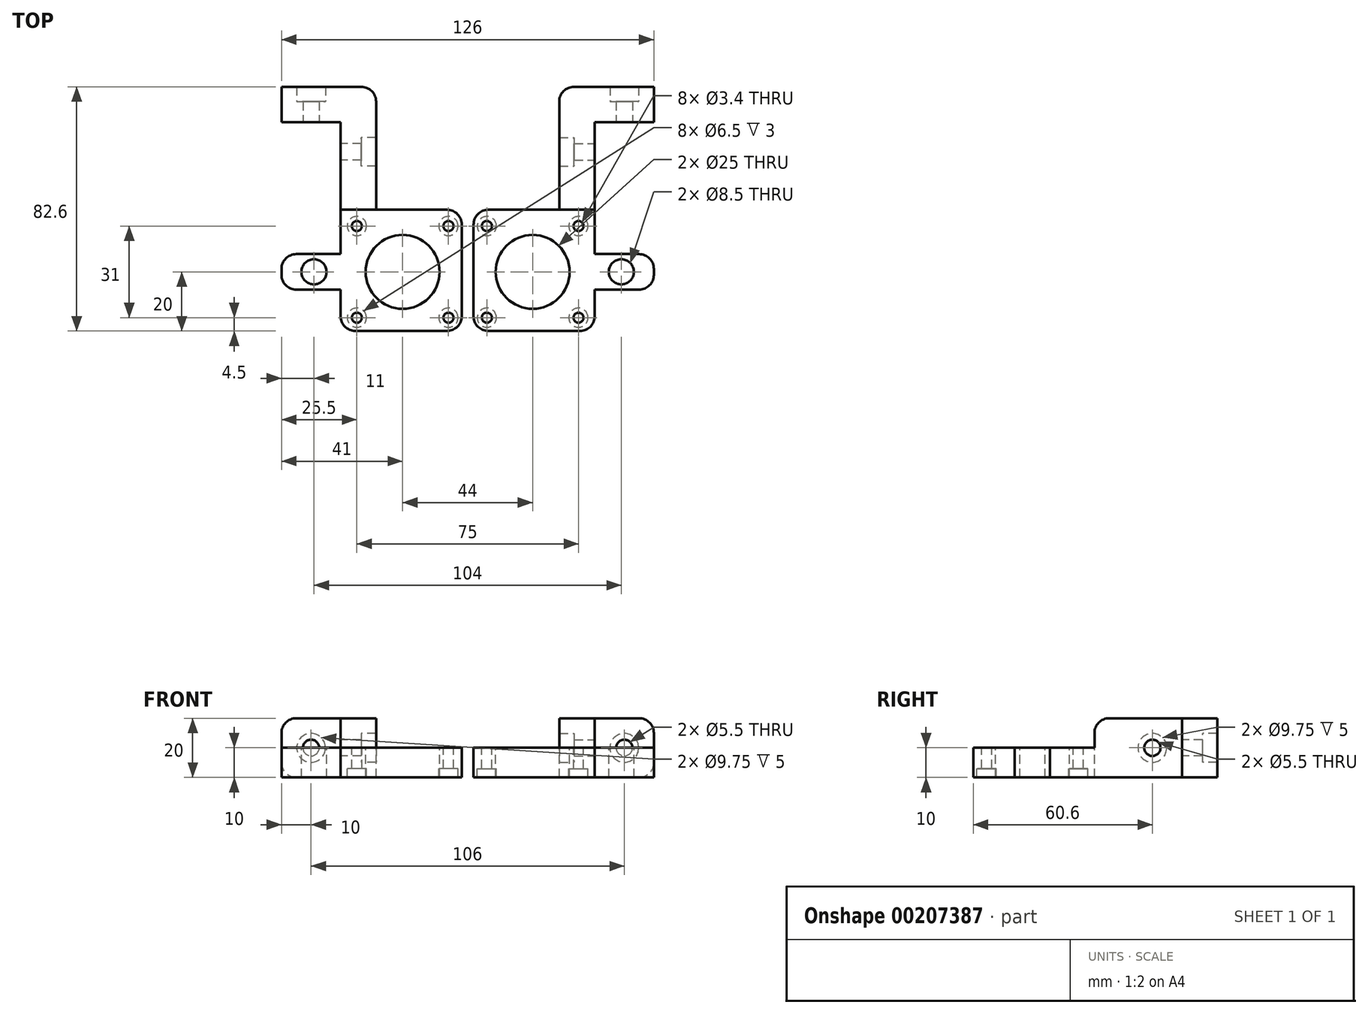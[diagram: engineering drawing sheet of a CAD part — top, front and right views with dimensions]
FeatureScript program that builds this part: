
annotation { "Feature Type Name" : "Feature", "Feature Type Description" : "" }
export const myFeature = defineFeature(function(context is Context, id is Id, definition is map)
    precondition{}
    {
        {
            var Q0;
            Q0=qCreatedBy(makeId("Top.planeOp"),FACE);
            var sketch = newSketch(context, id + "F0", { "sketchPlane" : qUnion([Q0])});
            skCircle(sketch, "E0", {"center": v(52, -6) * mm, "radius": 4.25 * mm});
            skPoint(sketch, "E1", {"position": v(6.5, 9.5) * mm});
            skPoint(sketch, "E2", {"position": v(37.5, 9.5) * mm});
            skPoint(sketch, "E3", {"position": v(6.5, -21.5) * mm});
            skPoint(sketch, "E4", {"position": v(37.5, -21.5) * mm});
            skLineSegment(sketch, "E5", {"start": v(6.5, 9.5) * mm, "end": v(37.5, -21.5) * mm, "construction": true});
            skLineSegment(sketch, "E6", {"start": v(6.5, -21.5) * mm, "end": v(37.5, 9.5) * mm, "construction": true});
            skPoint(sketch, "E7", {"position": v(22, -6) * mm});
            skPoint(sketch, "E8", {"position": v(43, -6) * mm});
            skLineSegment(sketch, "E9", {"start": v(43, 0) * mm, "end": v(43, -12) * mm});
            skLineSegment(sketch, "E10", {"start": v(43, -12) * mm, "end": v(63, -12) * mm});
            skLineSegment(sketch, "E11", {"start": v(31, -68.6) * mm, "end": v(31, -27) * mm});
            skLineSegment(sketch, "E12", {"start": v(43, 0) * mm, "end": v(43, 14) * mm});
            skLineSegment(sketch, "E13", {"start": v(43, 14) * mm, "end": v(2, 14) * mm});
            skLineSegment(sketch, "E14", {"start": v(43, -27) * mm, "end": v(43, -12) * mm});
            skCircle(sketch, "E15", {"center": v(22, -6) * mm, "radius": 12.5 * mm});
            skLineSegment(sketch, "E16", {"start": v(43, -27) * mm, "end": v(43, -56.6) * mm});
            skLineSegment(sketch, "E17", {"start": v(43, -56.6) * mm, "end": v(63, -56.6) * mm});
            skLineSegment(sketch, "E18", {"start": v(31, -27) * mm, "end": v(43, -27) * mm});
            skLineSegment(sketch, "E19", {"start": v(31, -27) * mm, "end": v(2, -27) * mm});
            skLineSegment(sketch, "E20", {"start": v(2, 14) * mm, "end": v(2, -27) * mm});
            skLineSegment(sketch, "E21", {"start": v(31, -68.6) * mm, "end": v(63, -68.6) * mm});
            skLineSegment(sketch, "E22", {"start": v(63, -68.6) * mm, "end": v(63, -56.6) * mm});
            skLineSegment(sketch, "E23", {"start": v(63, -12) * mm, "end": v(63, 0) * mm});
            skLineSegment(sketch, "E24", {"start": v(63, 0) * mm, "end": v(43, 0) * mm});
            skPoint(sketch, "E25", {"position": v(2, -6.5) * mm});
            skPoint(sketch, "E26", {"position": v(22.5, 14) * mm});
            skSolve(sketch);
        }
        {
            var Q0;
            Q0=makeQuery(id+"F0.imprint","IMPRINT",FACE,{"disambiguationData":[TD([[makeQuery(id+"F0.imprint","IMPRINT",EDGE,{"derivedFrom":sQuery(id+"F0.wireOp",EDGE,"E11")}),-1.0]])]});
            extrude(context, id + "F1", {"entities" : qUnion([Q0]), "depth" : 20 * mm, "offsetDistance" : 25 * mm});
        }
        {
            var Q0;
            Q0=makeQuery(id+"F0.imprint","IMPRINT",FACE,{"disambiguationData":[TD([[makeQuery(id+"F0.imprint","IMPRINT",EDGE,{"derivedFrom":sQuery(id+"F0.wireOp",EDGE,"E9")}),-1.0]])]});
            var Q1;
            Q1=makeQuery(id+"F0.imprint","IMPRINT",FACE,{"disambiguationData":[TD([[makeQuery(id+"F0.imprint","IMPRINT",EDGE,{"derivedFrom":sQuery(id+"F0.wireOp",EDGE,"E0")}),-1.0]])]});
            var Q2;
            Q2=makeQuery(id+"F1.opExtrude","CAP_FACE",FACE,{"disambiguationData":[OSD([sQuery(id+"F0.wireOp",EDGE,"ad533421-1adb-429a-b5a6-a6127de66475.right"),sQuery(id+"F0.wireOp",EDGE,"d9e2a834-b52d-49eb-9918-255f26fe5251.left"),sQuery(id+"F0.wireOp",EDGE,"d9e2a834-b52d-49eb-9918-255f26fe5251.right"),sQuery(id+"F0.wireOp",EDGE,"E0"),sQuery(id+"F0.wireOp",EDGE,"ce6baf13-d2b4-4efc-8f2e-d2ff027805c2.0.MirrorCS"),sQuery(id+"F0.wireOp",EDGE,"ce6baf13-d2b4-4efc-8f2e-d2ff027805c2.1.MirrorCS"),sQuery(id+"F0.wireOp",EDGE,"ce6baf13-d2b4-4efc-8f2e-d2ff027805c2.2.MirrorCS"),sQuery(id+"F0.wireOp",EDGE,"hfyD1Tr0-LGMV-87xt-wVYG-ZJ5qOrKsEWxK"),sQuery(id+"F0.wireOp",EDGE,"E9"),sQuery(id+"F0.wireOp",EDGE,"E10"),sQuery(id+"F0.wireOp",EDGE,"E11"),sQuery(id+"F0.wireOp",EDGE,"E16"),sQuery(id+"F0.wireOp",EDGE,"E17"),sQuery(id+"F0.wireOp",EDGE,"qAz9Y6s6-YjZz-jlty-H2bu-CIFENLusmMoC"),sQuery(id+"F0.wireOp",EDGE,"E18")])],"isStart":false});
            var Q3;
            Q3=makeQuery(id+"F1.opExtrude","SWEPT_BODY",BODY,{"disambiguationData":[OSD([sQuery(id+"F0.wireOp",EDGE,"ad533421-1adb-429a-b5a6-a6127de66475.right"),sQuery(id+"F0.wireOp",EDGE,"d9e2a834-b52d-49eb-9918-255f26fe5251.left"),sQuery(id+"F0.wireOp",EDGE,"d9e2a834-b52d-49eb-9918-255f26fe5251.right"),sQuery(id+"F0.wireOp",EDGE,"E0"),sQuery(id+"F0.wireOp",EDGE,"ce6baf13-d2b4-4efc-8f2e-d2ff027805c2.0.MirrorCS"),sQuery(id+"F0.wireOp",EDGE,"ce6baf13-d2b4-4efc-8f2e-d2ff027805c2.1.MirrorCS"),sQuery(id+"F0.wireOp",EDGE,"ce6baf13-d2b4-4efc-8f2e-d2ff027805c2.2.MirrorCS"),sQuery(id+"F0.wireOp",EDGE,"hfyD1Tr0-LGMV-87xt-wVYG-ZJ5qOrKsEWxK"),sQuery(id+"F0.wireOp",EDGE,"E9"),sQuery(id+"F0.wireOp",EDGE,"E10"),sQuery(id+"F0.wireOp",EDGE,"E11"),sQuery(id+"F0.wireOp",EDGE,"E16"),sQuery(id+"F0.wireOp",EDGE,"E17"),sQuery(id+"F0.wireOp",EDGE,"qAz9Y6s6-YjZz-jlty-H2bu-CIFENLusmMoC"),sQuery(id+"F0.wireOp",EDGE,"E18")])]});
            extrude(context, id + "F2", {"entities" : qUnion([Q0, Q1]), "operationType" : NewBodyOperationType.ADD, "depth" : 20 * mm, "endBoundEntityFace" : qUnion([Q2]), "endBoundEntityBody" : qUnion([Q3]), "offsetDistance" : -25 * mm, "offsetOppositeDirection" : true, "hasSecondDirection" : true, "secondDirectionOppositeDirection" : false, "secondDirectionDepth" : 10 * mm});
        }
        {
            var Q0;
            Q0=makeQuery(id+"F1.opExtrude","SWEPT_FACE",FACE,{"disambiguationData":[OSD([sQuery(id+"F0.wireOp",EDGE,"E11")])]});
            var sketch = newSketch(context, id + "F3", { "sketchPlane" : qUnion([Q0])});
            skPoint(sketch, "E27", {"position": v(26.6, 10) * mm});
            skPoint(sketch, "E28", {"position": v(46.6, 10) * mm});
            skPoint(sketch, "E29.0", {"position": v(6, 0) * mm});
            skSolve(sketch);
        }
        {
            var Q0;
            {var subQ0=sQuery(id+"F0.wireOp",EDGE,"E18");var subQ1=sQuery(id+"F0.wireOp",EDGE,"E9");Q0=makeQuery(id+"F2.boolean.opBoolean","MERGE",FACE,{"derivedFrom":[makeQuery(id+"F1.opExtrude","CAP_FACE",FACE,{"disambiguationData":[OSD([sQuery(id+"F0.wireOp",EDGE,"E0"),subQ1,sQuery(id+"F0.wireOp",EDGE,"E10"),sQuery(id+"F0.wireOp",EDGE,"E23"),sQuery(id+"F0.wireOp",EDGE,"E24")])],"isStart":false}),makeQuery(id+"F1.opExtrude","CAP_FACE",FACE,{"disambiguationData":[OSD([sQuery(id+"F0.wireOp",EDGE,"E11"),sQuery(id+"F0.wireOp",EDGE,"E16"),sQuery(id+"F0.wireOp",EDGE,"E17"),subQ0,sQuery(id+"F0.wireOp",EDGE,"E21"),sQuery(id+"F0.wireOp",EDGE,"E22")])],"isStart":false}),makeQuery(id+"F2.opExtrude","CAP_FACE",FACE,{"disambiguationData":[OSD([subQ1,sQuery(id+"F0.wireOp",EDGE,"E12"),sQuery(id+"F0.wireOp",EDGE,"E13"),sQuery(id+"F0.wireOp",EDGE,"E14"),sQuery(id+"F0.wireOp",EDGE,"E15"),subQ0,sQuery(id+"F0.wireOp",EDGE,"E19"),sQuery(id+"F0.wireOp",EDGE,"E20")])],"isStart":false})]});}
            var sketch = newSketch(context, id + "F4", { "sketchPlane" : qUnion([Q0])});
            skPoint(sketch, "E30.0", {"position": v(37.5, -21.5) * mm});
            skPoint(sketch, "E30.1", {"position": v(37.5, 9.5) * mm});
            skPoint(sketch, "E30.2", {"position": v(6.5, 9.5) * mm});
            skPoint(sketch, "E30.3", {"position": v(6.5, -21.5) * mm});
            skSolve(sketch);
        }
        {
            var Q0;
            Q0=makeQuery(id+"F1.opExtrude","SWEPT_FACE",FACE,{"disambiguationData":[OSD([sQuery(id+"F0.wireOp",EDGE,"E21")])]});
            var sketch = newSketch(context, id + "F5", { "sketchPlane" : qUnion([Q0])});
            skPoint(sketch, "E31", {"position": v(53, 10) * mm});
            skSolve(sketch);
        }
        {
            var Q0;
            Q0=sQuery(id+"F4.wireOp",VERTEX,"E30.2");
            var Q1;
            Q1=sQuery(id+"F4.wireOp",VERTEX,"E30.1");
            var Q2;
            Q2=sQuery(id+"F4.wireOp",VERTEX,"E30.0");
            var Q3;
            Q3=sQuery(id+"F4.wireOp",VERTEX,"E30.3");
            var Q4;
            Q4=makeQuery(id+"F1.opExtrude","SWEPT_BODY",BODY,{"disambiguationData":[OSD([sQuery(id+"F0.wireOp",EDGE,"E11"),sQuery(id+"F0.wireOp",EDGE,"E16"),sQuery(id+"F0.wireOp",EDGE,"E17"),sQuery(id+"F0.wireOp",EDGE,"E18"),sQuery(id+"F0.wireOp",EDGE,"E21"),sQuery(id+"F0.wireOp",EDGE,"E22")])]});
            hole(context, id + "F6", {"style" : HoleStyle.C_BORE, "endStyle" : HoleEndStyle.THROUGH, "standardTappedOrClearance" : lookupTablePath({ "fit" : "Normal", "standard" : "ISO", "size" : "M3", "type" : "Clearance" }), "standardBlindInLast" : lookupTablePath({ "fit" : "Normal", "standard" : "ISO", "engagement" : "75%", "pitch" : "0.5 mm", "size" : "M3", "type" : "Clearance & tapped" }), "holeDiameter" : 3.4 * mm, "cBoreDiameter" : 6.5 * mm, "cBoreDepth" : 3 * mm, "majorDiameter" : 5 * mm, "isTappedThrough" : true, "tappedDepth" : 12 * mm, "tapClearance" : 3, "locations" : qUnion([Q0, Q1, Q2, Q3]), "scope" : qUnion([Q4]), "startStyle" : HoleStartStyle.SKETCH});
        }
        {
            var Q0;
            Q0=sQuery(id+"F3.wireOp",VERTEX,"E28");
            var Q1;
            Q1=sQuery(id+"F5.wireOp",VERTEX,"E31");
            var Q2;
            Q2=sQuery(id+"FaZV30QIqoefiTR_1.wireOp",VERTEX,"a19fe755-67ef-45cf-8462-32ab6ddc702f.0");
            var Q3;
            Q3=sQuery(id+"FaZV30QIqoefiTR_1.wireOp",VERTEX,"29045288-7a21-441c-a3cb-12285636f115.0");
            var Q4;
            Q4=makeQuery(id+"F1.opExtrude","SWEPT_BODY",BODY,{"disambiguationData":[OSD([sQuery(id+"F0.wireOp",EDGE,"E11"),sQuery(id+"F0.wireOp",EDGE,"E16"),sQuery(id+"F0.wireOp",EDGE,"E17"),sQuery(id+"F0.wireOp",EDGE,"E18"),sQuery(id+"F0.wireOp",EDGE,"E21"),sQuery(id+"F0.wireOp",EDGE,"E22")])]});
            hole(context, id + "F7", {"style" : HoleStyle.C_BORE, "endStyle" : HoleEndStyle.BLIND, "standardTappedOrClearance" : lookupTablePath({ "fit" : "Normal", "standard" : "ISO", "size" : "M5", "type" : "Clearance" }), "standardBlindInLast" : lookupTablePath({ "fit" : "Normal", "standard" : "ISO", "engagement" : "75%", "pitch" : "0.8 mm", "size" : "M5", "type" : "Clearance & tapped" }), "holeDiameter" : 5.5 * mm, "cBoreDiameter" : 9.75 * mm, "cBoreDepth" : 5 * mm, "majorDiameter" : 5 * mm, "holeDepth" : 30 * mm, "isTappedThrough" : true, "tappedDepth" : 12 * mm, "tapClearance" : 3, "locations" : qUnion([Q0, Q1, Q2, Q3]), "scope" : qUnion([Q4]), "startStyle" : HoleStartStyle.SKETCH});
        }
        {
            var Q0;
            Q0=makeQuery(id+"F2.opExtrude","SWEPT_EDGE",EDGE,{"disambiguationData":[OSD([sQuery(id+"F0.wireOp",EDGE,"E13"),sQuery(id+"F0.wireOp",EDGE,"E20")])]});
            var Q1;
            Q1=makeQuery(id+"F2.opExtrude","SWEPT_EDGE",EDGE,{"disambiguationData":[OSD([sQuery(id+"F0.wireOp",EDGE,"E12"),sQuery(id+"F0.wireOp",EDGE,"E13")])]});
            var Q2;
            Q2=makeQuery(id+"F2.opExtrude","SWEPT_EDGE",EDGE,{"disambiguationData":[OSD([sQuery(id+"F0.wireOp",EDGE,"E19"),sQuery(id+"F0.wireOp",EDGE,"E20")])]});
            var Q3;
            Q3=makeQuery(id+"F2.opExtrude","SWEPT_EDGE",EDGE,{"disambiguationData":[OSD([sQuery(id+"F0.wireOp",EDGE,"E23"),sQuery(id+"F0.wireOp",EDGE,"E24")])]});
            var Q4;
            Q4=makeQuery(id+"F2.opExtrude","SWEPT_EDGE",EDGE,{"disambiguationData":[OSD([sQuery(id+"F0.wireOp",EDGE,"E10"),sQuery(id+"F0.wireOp",EDGE,"E23")])]});
            var Q5;
            Q5=makeQuery(id+"F1.opExtrude","CAP_EDGE",EDGE,{"disambiguationData":[OSD([sQuery(id+"F0.wireOp",EDGE,"E18")])],"isStart":true});
            var Q6;
            Q6=makeQuery(id+"F1.opExtrude","CAP_EDGE",EDGE,{"disambiguationData":[OSD([sQuery(id+"F0.wireOp",EDGE,"E22")])],"isStart":true});
            var Q7;
            Q7=makeQuery(id+"F1.opExtrude","CAP_EDGE",EDGE,{"disambiguationData":[OSD([sQuery(id+"F0.wireOp",EDGE,"E22")])],"isStart":false});
            var Q8;
            Q8=makeQuery(id+"F1.opExtrude","SWEPT_EDGE",EDGE,{"disambiguationData":[OSD([sQuery(id+"F0.wireOp",EDGE,"E11"),sQuery(id+"F0.wireOp",EDGE,"E21")])]});
            fillet(context, id + "F8", {"entities" : qUnion([Q0, Q1, Q2, Q3, Q4, Q5, Q6, Q7, Q8]), "radius" : 5 * mm, "tangentPropagation" : true, "allowEdgeOverflow" : false});
        }
        {
            var Q0;
            Q0=makeQuery(id+"F1.opExtrude","SWEPT_BODY",BODY,{"disambiguationData":[OSD([sQuery(id+"F0.wireOp",EDGE,"E11"),sQuery(id+"F0.wireOp",EDGE,"E16"),sQuery(id+"F0.wireOp",EDGE,"E17"),sQuery(id+"F0.wireOp",EDGE,"E18"),sQuery(id+"F0.wireOp",EDGE,"E21"),sQuery(id+"F0.wireOp",EDGE,"E22")])]});
            var Q1;
            Q1=makeQuery(id+"F2.opExtrude","CAP_EDGE",EDGE,{"disambiguationData":[OSD([sQuery(id+"F0.wireOp",EDGE,"E13")])],"isStart":false});
            transform(context, id + "F9", {"entities" : qUnion([Q0]), "transformType" : TransformType.ROTATION, "transformAxis" : qUnion([Q1]), "angle" : 180 * degree, "makeCopy" : false});
        }
        {
            var Q0;
            Q0=makeQuery(id+"F1.opExtrude","SWEPT_BODY",BODY,{"disambiguationData":[OSD([sQuery(id+"F0.wireOp",EDGE,"E11"),sQuery(id+"F0.wireOp",EDGE,"E16"),sQuery(id+"F0.wireOp",EDGE,"E17"),sQuery(id+"F0.wireOp",EDGE,"E18"),sQuery(id+"F0.wireOp",EDGE,"E21"),sQuery(id+"F0.wireOp",EDGE,"E22")])]});
            var Q1;
            Q1=qCreatedBy(makeId("Right.planeOp"),FACE);
            mirror(context, id + "F10", {"entities" : qUnion([Q0]), "mirrorPlane" : qUnion([Q1])});
        }
    });
